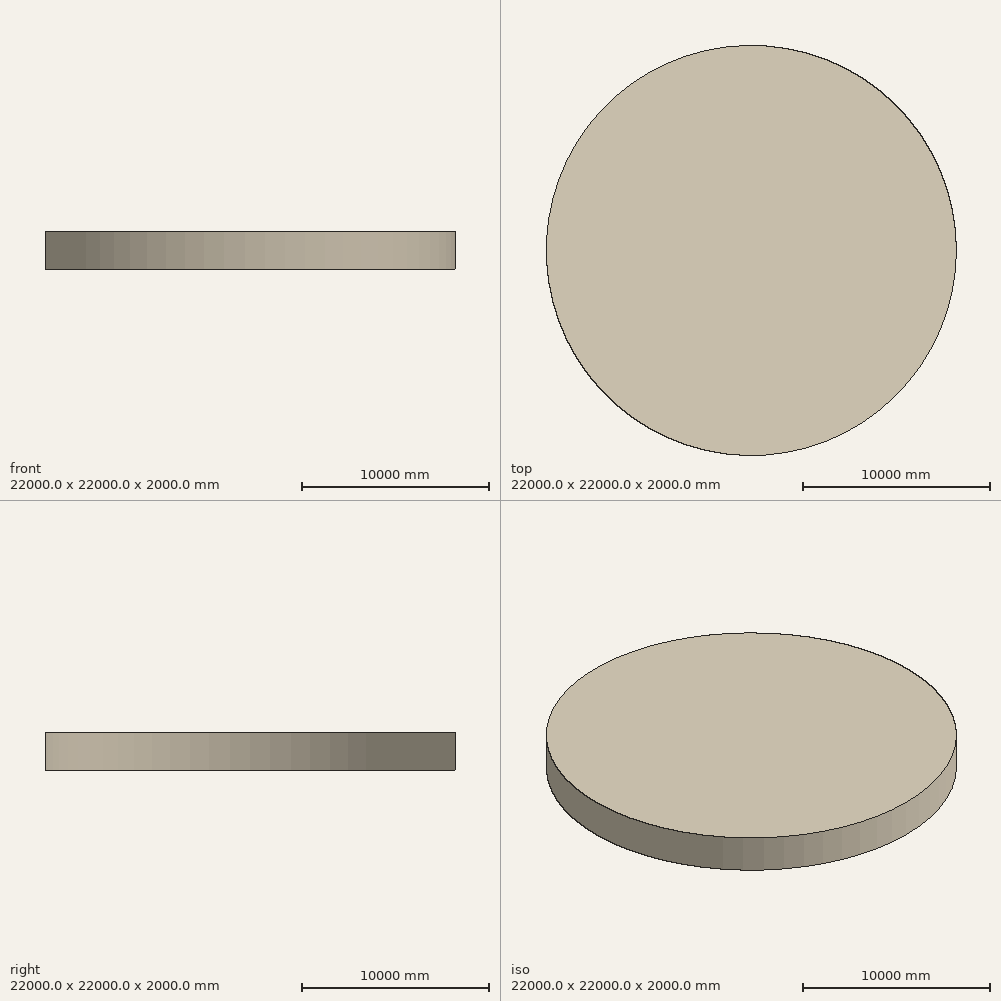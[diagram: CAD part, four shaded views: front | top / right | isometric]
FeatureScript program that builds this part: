
annotation { "Feature Type Name" : "Feature", "Feature Type Description" : "" }
export const myFeature = defineFeature(function(context is Context, id is Id, definition is map)
    precondition{}
    {
        {
            var Q0;
            Q0=qCreatedBy(makeId("Top.planeOp"),FACE);
            cPlane(context, id + "F0", {"entities" : qUnion([Q0]), "cplaneType" : CPlaneType.OFFSET, "offset" : 0 * mm, "width" : 152.4 * mm, "height" : 152.4 * mm});
        }
        {
            var Q0;
            Q0=qCreatedBy(id+"F0.planeOp",FACE);
            var sketch = newSketch(context, id + "F1", { "sketchPlane" : qUnion([Q0])});
            skCircle(sketch, "E0", {"center": v(0, 0) * mm, "radius": 11000 * mm});
            skSolve(sketch);
        }
        {
            var Q0;
            Q0 = qSketchRegion(id + "F1", true);
            extrude(context, id + "F2", {"entities" : qUnion([Q0]), "depth" : 2000 * mm});
        }
    });
